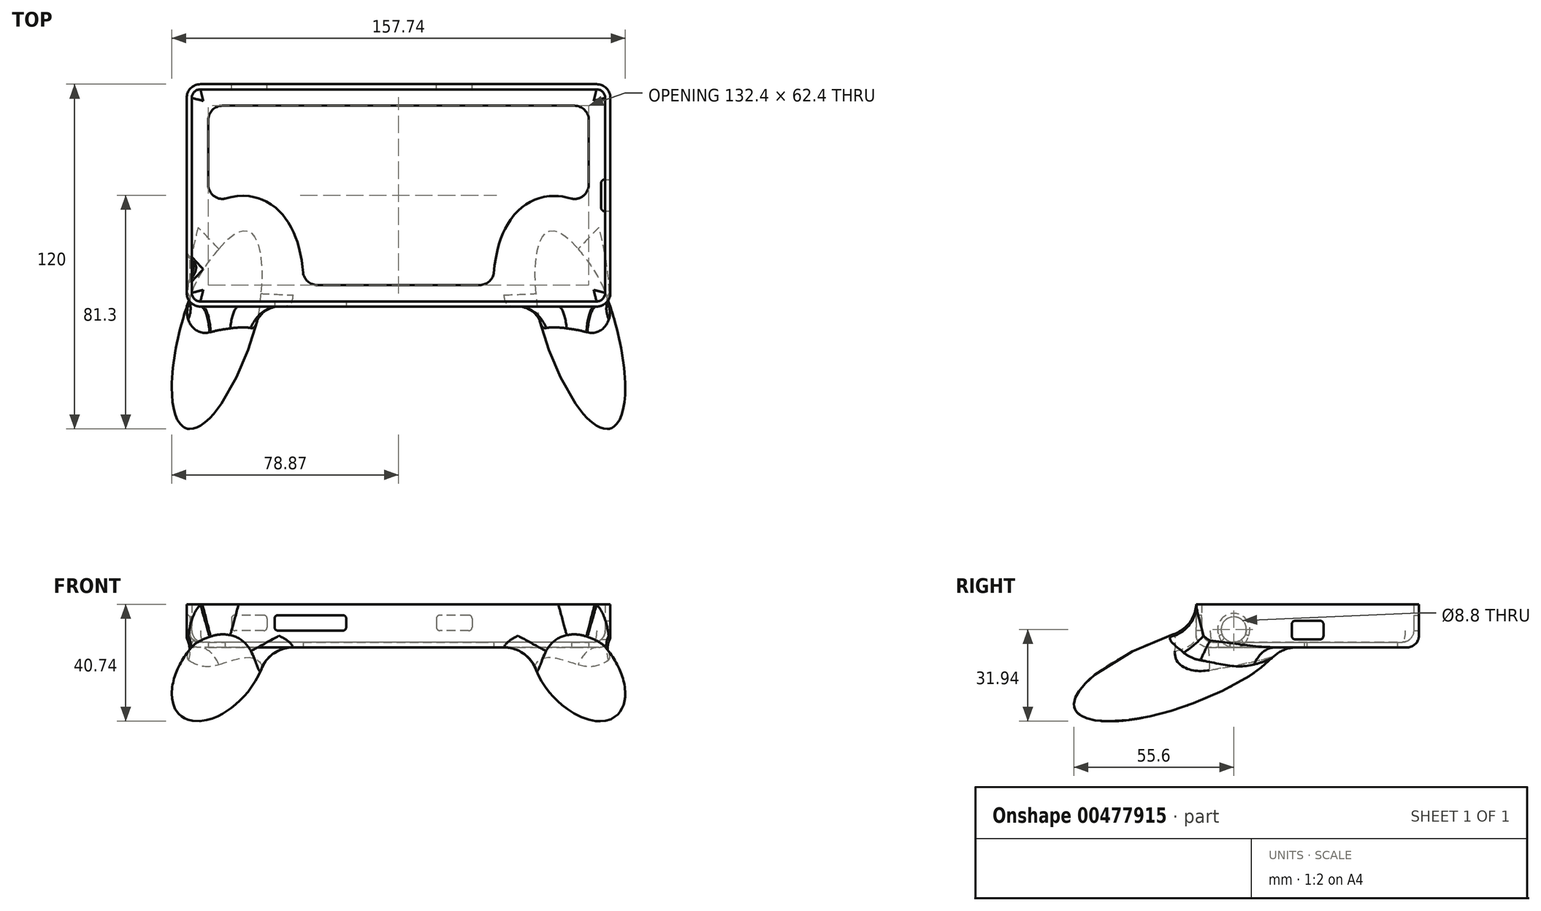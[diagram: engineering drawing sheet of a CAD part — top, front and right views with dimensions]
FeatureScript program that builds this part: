
annotation { "Feature Type Name" : "Feature", "Feature Type Description" : "" }
export const myFeature = defineFeature(function(context is Context, id is Id, definition is map)
    precondition{}
    {
        {
            var Q0;
            Q0=qCreatedBy(makeId("Top.planeOp"),FACE);
            var sketch = newSketch(context, id + "F0", { "sketchPlane" : qUnion([Q0])});
            skLineSegment(sketch, "E0.bottom", {"start": v(68.9, -36.9) * mm, "end": v(-68.9, -36.9) * mm});
            skLineSegment(sketch, "E0.top", {"start": v(68.9, 36.9) * mm, "end": v(-68.9, 36.9) * mm});
            skLineSegment(sketch, "E0.left", {"start": v(71.9, -33.9) * mm, "end": v(71.9, 33.9) * mm});
            skLineSegment(sketch, "E0.right", {"start": v(-71.9, -33.9) * mm, "end": v(-71.9, 33.9) * mm});
            skPoint(sketch, "E0.middle", {"position": v(0, 0) * mm});
            skLineSegment(sketch, "E1.bottom", {"start": v(-56.9, 37.9) * mm, "end": v(-46.9, 37.9) * mm});
            skLineSegment(sketch, "E1.top", {"start": v(-56.9, 36.9) * mm, "end": v(-46.9, 36.9) * mm});
            skLineSegment(sketch, "E1.left", {"start": v(-56.9, 37.9) * mm, "end": v(-56.9, 36.9) * mm});
            skLineSegment(sketch, "E1.right", {"start": v(-46.9, 37.9) * mm, "end": v(-46.9, 36.9) * mm});
            skLineSegment(sketch, "E2.bottom", {"start": v(14.4, 37.9) * mm, "end": v(24.4, 37.9) * mm});
            skLineSegment(sketch, "E2.top", {"start": v(14.4, 36.9) * mm, "end": v(24.4, 36.9) * mm});
            skLineSegment(sketch, "E2.left", {"start": v(14.4, 37.9) * mm, "end": v(14.4, 36.9) * mm});
            skLineSegment(sketch, "E2.right", {"start": v(24.4, 37.9) * mm, "end": v(24.4, 36.9) * mm});
            skLineSegment(sketch, "E3.bottom", {"start": v(-41.9, -36.9) * mm, "end": v(-19.4, -36.9) * mm});
            skLineSegment(sketch, "E3.top", {"start": v(-41.9, -37.9) * mm, "end": v(-19.4, -37.9) * mm});
            skLineSegment(sketch, "E3.left", {"start": v(-41.9, -36.9) * mm, "end": v(-41.9, -37.9) * mm});
            skLineSegment(sketch, "E3.right", {"start": v(-19.4, -36.9) * mm, "end": v(-19.4, -37.9) * mm});
            skPoint(sketch, "E4.visualSharp", {"position": v(71.9, 36.9) * mm});
            skArc(sketch, "E4.filletArc", {"start": v(71.9, 33.9) * mm, "mid": v(71.02, 36.02) * mm, "end": v(68.9, 36.9) * mm});
            skPoint(sketch, "E5.visualSharp", {"position": v(-71.9, 36.9) * mm});
            skArc(sketch, "E5.filletArc", {"start": v(-68.9, 36.9) * mm, "mid": v(-71.02, 36.02) * mm, "end": v(-71.9, 33.9) * mm});
            skPoint(sketch, "E6.visualSharp", {"position": v(-71.9, -36.9) * mm});
            skArc(sketch, "E6.filletArc", {"start": v(-71.9, -33.9) * mm, "mid": v(-71.02, -36.02) * mm, "end": v(-68.9, -36.9) * mm});
            skPoint(sketch, "E7.visualSharp", {"position": v(71.9, -36.9) * mm});
            skArc(sketch, "E7.filletArc", {"start": v(68.9, -36.9) * mm, "mid": v(71.02, -36.02) * mm, "end": v(71.9, -33.9) * mm});
            skSolve(sketch);
        }
        {
            var Q0;
            Q0=qCreatedBy(makeId("Top.planeOp"),FACE);
            var sketch = newSketch(context, id + "F1", { "sketchPlane" : qUnion([Q0])});
            skLineSegment(sketch, "E8", {"start": v(-71.9, -33.9) * mm, "end": v(-57.84, 4.74) * mm, "construction": true});
            skLineSegment(sketch, "E9", {"start": v(-73.64, -83.73) * mm, "end": v(-51.33, -6.9) * mm});
            skEllipticalArc(sketch, "E10", {});
            skEllipticalArc(sketch, "E11", {"construction": true});
            skEllipticalArc(sketch, "E12.MirrorCS", {});
            skLineSegment(sketch, "E13.MirrorCS", {"start": v(73.64, -83.73) * mm, "end": v(51.33, -6.9) * mm});
            skEllipticalArc(sketch, "E14.MirrorCS", {"construction": true});
            const initialGuessF1  = {"E10": [-0.062483445005433624, -0.045313524145155444, -0.27883817299371894, -0.960338103628886, 0.04, 0.0125, 3.141592653589793, 0], "E11": [-0.06248344500543363, -0.045313524145155444, -0.27883817299371894, -0.960338103628886, 0.04, 0.0125, 0, 3.141592653589793], "E12.MirrorCS": [0.06248344500543363, -0.045313524145155444, 0.27883817299371894, -0.960338103628886, 0.04, 0.0125, 0, 3.141592653589793], "E14.MirrorCS": [0.06248344500543364, -0.045313524145155444, 0.27883817299371894, -0.960338103628886, 0.04, 0.0125, 3.141592653589793, 0]};
            skSetInitialGuess(sketch, initialGuessF1);
            skSolve(sketch);
        }
        {
            var Q0;
            Q0=makeQuery(id+"F1.imprint","IMPRINT",FACE,{"disambiguationData":[TD([[makeQuery(id+"F1.imprint","IMPRINT",EDGE,{"derivedFrom":sQuery(id+"F1.wireOp",EDGE,"E9")}),1.0]])]});
            var Q1;
            Q1=sQuery(id+"F1.wireOp",EDGE,"E9");
            revolve(context, id + "F2", {"entities" : qUnion([Q0]), "axis" : qUnion([Q1]), "revolveType" : RevolveType.FULL});
        }
        {
            var Q0;
            Q0=makeQuery(id+"F1.imprint","IMPRINT",FACE,{"disambiguationData":[TD([[makeQuery(id+"F1.imprint","IMPRINT",EDGE,{"derivedFrom":sQuery(id+"F1.wireOp",EDGE,"E12.MirrorCS")}),1.0]])]});
            var Q1;
            Q1=sQuery(id+"F1.wireOp",EDGE,"E13.MirrorCS");
            revolve(context, id + "F3", {"entities" : qUnion([Q0]), "axis" : qUnion([Q1]), "revolveType" : RevolveType.FULL});
        }
        {
            var Q0;
            Q0=makeQuery(id+"F3.opRevolve","SWEPT_BODY",BODY,{"disambiguationData":[OSD([sQuery(id+"F1.wireOp",EDGE,"E12.MirrorCS"),sQuery(id+"F1.wireOp",EDGE,"E13.MirrorCS")])]});
            var Q1;
            Q1=makeQuery(id+"F2.opRevolve","SWEPT_BODY",BODY,{"disambiguationData":[OSD([sQuery(id+"F1.wireOp",EDGE,"E9"),sQuery(id+"F1.wireOp",EDGE,"E10")])]});
            var Q2;
            Q2=sQuery(id+"F0.wireOp",EDGE,"E0.bottom");
            transform(context, id + "F4", {"entities" : qUnion([Q0, Q1]), "transformType" : TransformType.ROTATION, "transformAxis" : qUnion([Q2]), "angle" : 20 * degree, "oppositeDirection" : true, "makeCopy" : false});
        }
        {
            var Q0;
            Q0=makeQuery(id+"F2.opRevolve","SWEPT_BODY",BODY,{"disambiguationData":[OSD([sQuery(id+"F1.wireOp",EDGE,"E9"),sQuery(id+"F1.wireOp",EDGE,"E10")])]});
            var Q1;
            Q1=makeQuery(id+"F3.opRevolve","SWEPT_BODY",BODY,{"disambiguationData":[OSD([sQuery(id+"F1.wireOp",EDGE,"E12.MirrorCS"),sQuery(id+"F1.wireOp",EDGE,"E13.MirrorCS")])]});
            transform(context, id + "F5", {"entities" : qUnion([Q0, Q1]), "transformType" : TransformType.TRANSLATION_3D, "dx" : 0 * mm, "dy" : 0 * mm, "dz" : -7 * mm, "makeCopy" : false});
        }
        {
            var Q0;
            {var subQ3=sQuery(id+"F0.wireOp",EDGE,"E0.left");Q0=makeQuery(id+"F0.imprint","IMPRINT",FACE,{"disambiguationData":[TD([[makeQuery(id+"F0.imprint","IMPRINT",EDGE,{"derivedFrom":subQ3}),1.0]])]});}
            extrude(context, id + "F6", {"entities" : qUnion([Q0]), "depth" : 13.2 * mm});
        }
        {
            var Q0;
            {var subQ3=sQuery(id+"F0.wireOp",EDGE,"E0.left");Q0=makeQuery(id+"F0.imprint","IMPRINT",FACE,{"disambiguationData":[TD([[makeQuery(id+"F0.imprint","IMPRINT",EDGE,{"derivedFrom":subQ3}),1.0]])]});}
            var sketch = newSketch(context, id + "F7", { "sketchPlane" : qUnion([Q0])});
            skArc(sketch, "E15.0", {"start": v(73.7, 33.9) * mm, "mid": v(72.3, 37.3) * mm, "end": v(68.9, 38.7) * mm});
            skLineSegment(sketch, "E15.1", {"start": v(73.7, -33.9) * mm, "end": v(73.7, 33.9) * mm});
            skLineSegment(sketch, "E15.2", {"start": v(68.9, 38.7) * mm, "end": v(-68.9, 38.7) * mm});
            skArc(sketch, "E15.3", {"start": v(68.9, -38.7) * mm, "mid": v(72.3, -37.3) * mm, "end": v(73.7, -33.9) * mm});
            skArc(sketch, "E15.4", {"start": v(-68.9, 38.7) * mm, "mid": v(-72.3, 37.3) * mm, "end": v(-73.7, 33.9) * mm});
            skLineSegment(sketch, "E15.5", {"start": v(-73.7, -33.9) * mm, "end": v(-73.7, 33.9) * mm});
            skArc(sketch, "E15.6", {"start": v(-73.7, -33.9) * mm, "mid": v(-72.3, -37.3) * mm, "end": v(-68.9, -38.7) * mm});
            skLineSegment(sketch, "E15.7", {"start": v(68.9, -38.7) * mm, "end": v(-68.9, -38.7) * mm});
            skSolve(sketch);
        }
        {
            var Q0;
            Q0 = qSketchRegion(id + "F7", true);
            var Q1;
            Q1=makeQuery(id+"F6.opExtrude","CAP_FACE",FACE,{"disambiguationData":[OSD([sQuery(id+"F0.wireOp",EDGE,"E0.bottom"),sQuery(id+"F0.wireOp",EDGE,"E0.top"),sQuery(id+"F0.wireOp",EDGE,"E0.left"),sQuery(id+"F0.wireOp",EDGE,"E0.right"),sQuery(id+"F0.wireOp",EDGE,"E1.top"),sQuery(id+"F0.wireOp",EDGE,"E2.top"),sQuery(id+"F0.wireOp",EDGE,"E3.bottom"),sQuery(id+"F0.wireOp",EDGE,"E4.filletArc"),sQuery(id+"F0.wireOp",EDGE,"E5.filletArc"),sQuery(id+"F0.wireOp",EDGE,"E6.filletArc"),sQuery(id+"F0.wireOp",EDGE,"E7.filletArc")])],"isStart":false});
            extrude(context, id + "F8", {"entities" : qUnion([Q0]), "endBound" : BoundingType.UP_TO_SURFACE, "endBoundEntityFace" : qUnion([Q1]), "depth" : 13 * mm, "hasSecondDirection" : true, "secondDirectionOppositeDirection" : true, "secondDirectionDepth" : 1.8 * mm});
        }
        {
            var Q0;
            Q0=makeQuery(id+"F2.opRevolve","SWEPT_BODY",BODY,{"disambiguationData":[OSD([sQuery(id+"F1.wireOp",EDGE,"E9"),sQuery(id+"F1.wireOp",EDGE,"E10")])]});
            var Q1;
            Q1=makeQuery(id+"F3.opRevolve","SWEPT_BODY",BODY,{"disambiguationData":[OSD([sQuery(id+"F1.wireOp",EDGE,"E12.MirrorCS"),sQuery(id+"F1.wireOp",EDGE,"E13.MirrorCS")])]});
            var Q2;
            Q2=makeQuery(id+"F8.opExtrude","SWEPT_BODY",BODY,{"disambiguationData":[OSD([sQuery(id+"F7.wireOp",EDGE,"E15.0"),sQuery(id+"F7.wireOp",EDGE,"E15.1"),sQuery(id+"F7.wireOp",EDGE,"E15.2"),sQuery(id+"F7.wireOp",EDGE,"E15.3"),sQuery(id+"F7.wireOp",EDGE,"E15.4"),sQuery(id+"F7.wireOp",EDGE,"E15.5"),sQuery(id+"F7.wireOp",EDGE,"E15.6"),sQuery(id+"F7.wireOp",EDGE,"E15.7")])]});
            booleanBodies(context, id + "F9", {"operationType" : BooleanOperationType.UNION, "tools" : qUnion([Q0, Q1, Q2])});
        }
        {
            var Q0;
            Q0=makeQuery(id+"F6.opExtrude","SWEPT_BODY",BODY,{"disambiguationData":[OSD([sQuery(id+"F0.wireOp",EDGE,"E0.bottom"),sQuery(id+"F0.wireOp",EDGE,"E0.top"),sQuery(id+"F0.wireOp",EDGE,"E0.left"),sQuery(id+"F0.wireOp",EDGE,"E0.right"),sQuery(id+"F0.wireOp",EDGE,"E1.top"),sQuery(id+"F0.wireOp",EDGE,"E2.top"),sQuery(id+"F0.wireOp",EDGE,"E3.bottom"),sQuery(id+"F0.wireOp",EDGE,"E4.filletArc"),sQuery(id+"F0.wireOp",EDGE,"E5.filletArc"),sQuery(id+"F0.wireOp",EDGE,"E6.filletArc"),sQuery(id+"F0.wireOp",EDGE,"E7.filletArc")])]});
            var Q1;
            Q1=makeQuery(id+"F2.opRevolve","SWEPT_BODY",BODY,{"disambiguationData":[OSD([sQuery(id+"F1.wireOp",EDGE,"E9"),sQuery(id+"F1.wireOp",EDGE,"E10")])]});
            var Q2;
            Q2=makeQuery(id+"F3.opRevolve","SWEPT_BODY",BODY,{"disambiguationData":[OSD([sQuery(id+"F1.wireOp",EDGE,"E12.MirrorCS"),sQuery(id+"F1.wireOp",EDGE,"E13.MirrorCS")])]});
            var Q3;
            Q3=makeQuery(id+"F8.opExtrude","SWEPT_BODY",BODY,{"disambiguationData":[OSD([sQuery(id+"F7.wireOp",EDGE,"E15.0"),sQuery(id+"F7.wireOp",EDGE,"E15.1"),sQuery(id+"F7.wireOp",EDGE,"E15.2"),sQuery(id+"F7.wireOp",EDGE,"E15.3"),sQuery(id+"F7.wireOp",EDGE,"E15.4"),sQuery(id+"F7.wireOp",EDGE,"E15.5"),sQuery(id+"F7.wireOp",EDGE,"E15.6"),sQuery(id+"F7.wireOp",EDGE,"E15.7")])]});
            booleanBodies(context, id + "F10", {"operationType" : BooleanOperationType.SUBTRACTION, "tools" : qUnion([Q0]), "targets" : qUnion([Q1, Q2, Q3])});
        }
        {
            var Q0;
            Q0=makeQuery(id+"F10.opBoolean","COPY",FACE,{"derivedFrom":makeQuery(id+"F6.opExtrude","CAP_FACE",FACE,{"disambiguationData":[OSD([sQuery(id+"F0.wireOp",EDGE,"E0.bottom"),sQuery(id+"F0.wireOp",EDGE,"E0.top"),sQuery(id+"F0.wireOp",EDGE,"E0.left"),sQuery(id+"F0.wireOp",EDGE,"E0.right"),sQuery(id+"F0.wireOp",EDGE,"E1.top"),sQuery(id+"F0.wireOp",EDGE,"E2.top"),sQuery(id+"F0.wireOp",EDGE,"E3.bottom"),sQuery(id+"F0.wireOp",EDGE,"E4.filletArc"),sQuery(id+"F0.wireOp",EDGE,"E5.filletArc"),sQuery(id+"F0.wireOp",EDGE,"E6.filletArc"),sQuery(id+"F0.wireOp",EDGE,"E7.filletArc")])],"isStart":true})});
            var Q1;
            Q1=makeQuery(id+"F8.opExtrude","CAP_EDGE",EDGE,{"disambiguationData":[OSD([sQuery(id+"F7.wireOp",EDGE,"E15.7")])],"isStart":true});
            var Q2;
            Q2=makeQuery(id+"F8.opExtrude","CAP_EDGE",EDGE,{"disambiguationData":[OSD([sQuery(id+"F7.wireOp",EDGE,"E15.2")])],"isStart":true});
            fillet(context, id + "F11", {"entities" : qUnion([Q0, Q1, Q2]), "radius" : 4 * mm, "tangentPropagation" : true, "allowEdgeOverflow" : false});
        }
        {
            var Q0;
            Q0=makeQuery(id+"F9.opBoolean","INTERSECT",EDGE,{"derivedFrom":[makeQuery(id+"F2.opRevolve","SWEPT_FACE",FACE,{"disambiguationData":[OSD([sQuery(id+"F1.wireOp",EDGE,"E10")])]}),makeQuery(id+"F8.opExtrude","CAP_FACE",FACE,{"disambiguationData":[OSD([sQuery(id+"F7.wireOp",EDGE,"E15.0"),sQuery(id+"F7.wireOp",EDGE,"E15.1"),sQuery(id+"F7.wireOp",EDGE,"E15.2"),sQuery(id+"F7.wireOp",EDGE,"E15.3"),sQuery(id+"F7.wireOp",EDGE,"E15.4"),sQuery(id+"F7.wireOp",EDGE,"E15.5"),sQuery(id+"F7.wireOp",EDGE,"E15.6"),sQuery(id+"F7.wireOp",EDGE,"E15.7")])],"isStart":true})]});
            var Q1;
            Q1=makeQuery(id+"F9.opBoolean","INTERSECT",EDGE,{"derivedFrom":[makeQuery(id+"F3.opRevolve","SWEPT_FACE",FACE,{"disambiguationData":[OSD([sQuery(id+"F1.wireOp",EDGE,"E12.MirrorCS")])]}),makeQuery(id+"F8.opExtrude","CAP_FACE",FACE,{"disambiguationData":[OSD([sQuery(id+"F7.wireOp",EDGE,"E15.0"),sQuery(id+"F7.wireOp",EDGE,"E15.1"),sQuery(id+"F7.wireOp",EDGE,"E15.2"),sQuery(id+"F7.wireOp",EDGE,"E15.3"),sQuery(id+"F7.wireOp",EDGE,"E15.4"),sQuery(id+"F7.wireOp",EDGE,"E15.5"),sQuery(id+"F7.wireOp",EDGE,"E15.6"),sQuery(id+"F7.wireOp",EDGE,"E15.7")])],"isStart":true})]});
            fillet(context, id + "F12", {"entities" : qUnion([Q0, Q1]), "radius" : 12 * mm, "tangentPropagation" : true, "allowEdgeOverflow" : false});
        }
        {
            var Q0;
            Q0=makeQuery(id+"F8.opExtrude","CAP_FACE",FACE,{"disambiguationData":[OSD([sQuery(id+"F7.wireOp",EDGE,"E15.0"),sQuery(id+"F7.wireOp",EDGE,"E15.1"),sQuery(id+"F7.wireOp",EDGE,"E15.2"),sQuery(id+"F7.wireOp",EDGE,"E15.3"),sQuery(id+"F7.wireOp",EDGE,"E15.4"),sQuery(id+"F7.wireOp",EDGE,"E15.5"),sQuery(id+"F7.wireOp",EDGE,"E15.6"),sQuery(id+"F7.wireOp",EDGE,"E15.7")])],"isStart":true});
            var sketch = newSketch(context, id + "F13", { "sketchPlane" : qUnion([Q0])});
            skLineSegment(sketch, "E16.0", {"start": v(66.2, -26.2) * mm, "end": v(66.2, -3.77) * mm});
            skLineSegment(sketch, "E16.1", {"start": v(28.26, 31.2) * mm, "end": v(-28.26, 31.2) * mm});
            skFitSpline(sketch, "E16.2", {"points": [v(-33.12, 34.86) * mm, v(-33.06, 33.6) * mm, v(-33.02, 31.71) * mm, v(-33.08, 29.18) * mm, v(-33.18, 27.27) * mm, v(-33.35, 25.36) * mm, v(-33.66, 22.82) * mm, v(-34.11, 20.28) * mm, v(-34.75, 17.76) * mm, v(-35.23, 16.18) * mm, v(-35.67, 14.92) * mm, v(-36.16, 13.66) * mm, v(-36.84, 12.11) * mm, v(-37.8, 10.3) * mm, v(-38.73, 8.83) * mm, v(-39.56, 7.7) * mm, v(-40.24, 6.85) * mm, v(-40.96, 6.05) * mm, v(-41.97, 5.01) * mm, v(-43.36, 3.82) * mm, v(-44.91, 2.77) * mm, v(-46.23, 2.05) * mm, v(-47.24, 1.58) * mm, v(-48.29, 1.17) * mm, v(-49.36, 0.83) * mm, v(-50.47, 0.56) * mm, v(-51.95, 0.3) * mm, v(-53.8, 0.15) * mm, v(-56, 0.24) * mm, v(-58.17, 0.58) * mm, v(-60.25, 1.13) * mm, v(-62.22, 1.86) * mm, v(-64.12, 2.75) * mm, v(-65.9, 3.76) * mm, v(-67.58, 4.86) * mm, v(-69.7, 6.44) * mm, v(-71.18, 7.74) * mm, v(-72.12, 8.65) * mm]});
            skFitSpline(sketch, "E16.3", {"points": [v(72.12, 8.65) * mm, v(71.65, 8.2) * mm, v(70.69, 7.3) * mm, v(69.17, 6.04) * mm, v(67.56, 4.85) * mm, v(65.86, 3.73) * mm, v(64.07, 2.73) * mm, v(62.2, 1.85) * mm, v(60.56, 1.25) * mm, v(59.18, 0.85) * mm, v(58.12, 0.6) * mm, v(57.05, 0.4) * mm, v(55.97, 0.27) * mm, v(54.87, 0.2) * mm, v(53.75, 0.18) * mm, v(52.62, 0.24) * mm, v(51.13, 0.42) * mm, v(49.67, 0.73) * mm, v(48.24, 1.19) * mm, v(47.19, 1.6) * mm, v(46.16, 2.09) * mm, v(44.85, 2.8) * mm, v(43.63, 3.64) * mm, v(42.49, 4.57) * mm, v(41.4, 5.56) * mm, v(40.18, 6.88) * mm, v(38.9, 8.56) * mm, v(37.97, 10.03) * mm, v(37.3, 11.25) * mm, v(36.68, 12.47) * mm, v(36, 14.02) * mm, v(35.31, 15.9) * mm, v(34.74, 17.8) * mm, v(34.1, 20.35) * mm, v(33.53, 23.52) * mm, v(33.15, 27.31) * mm, v(33.01, 31.09) * mm, v(33.06, 33.6) * mm, v(33.12, 34.86) * mm]});
            skLineSegment(sketch, "E16.4", {"start": v(-66.2, -3.77) * mm, "end": v(-66.2, -26.2) * mm});
            skLineSegment(sketch, "E16.5", {"start": v(-61.2, -31.2) * mm, "end": v(61.2, -31.2) * mm});
            skPoint(sketch, "E17.visualSharp", {"position": v(66.2, -31.2) * mm});
            skArc(sketch, "E17.filletArc", {"start": v(61.2, -31.2) * mm, "mid": v(64.74, -29.74) * mm, "end": v(66.2, -26.2) * mm});
            skPoint(sketch, "E18.visualSharp", {"position": v(-66.2, -31.2) * mm});
            skArc(sketch, "E18.filletArc", {"start": v(-66.2, -26.2) * mm, "mid": v(-64.74, -29.74) * mm, "end": v(-61.2, -31.2) * mm});
            skPoint(sketch, "E19.visualSharp", {"position": v(-66.2, 3.97) * mm});
            skArc(sketch, "E19.filletArc", {"start": v(-59.79, 1.03) * mm, "mid": v(-64.2, 0.23) * mm, "end": v(-66.2, -3.77) * mm});
            skPoint(sketch, "E20.visualSharp", {"position": v(-33.05, 31.2) * mm});
            skArc(sketch, "E20.filletArc", {"start": v(-28.26, 31.2) * mm, "mid": v(-31.65, 29.88) * mm, "end": v(-33.24, 26.6) * mm});
            skPoint(sketch, "E21.visualSharp", {"position": v(33.05, 31.2) * mm});
            skArc(sketch, "E21.filletArc", {"start": v(33.24, 26.6) * mm, "mid": v(31.65, 29.88) * mm, "end": v(28.26, 31.2) * mm});
            skPoint(sketch, "E22.visualSharp", {"position": v(66.2, 3.97) * mm});
            skArc(sketch, "E22.filletArc", {"start": v(66.2, -3.77) * mm, "mid": v(64.2, 0.23) * mm, "end": v(59.79, 1.03) * mm});
            skSolve(sketch);
        }
        {
            var Q0;
            Q0=makeQuery(id+"F13.imprint","IMPRINT",FACE,{"disambiguationData":[TD([[makeQuery(id+"F13.imprint","IMPRINT",EDGE,{"derivedFrom":sQuery(id+"F13.wireOp",EDGE,"E16.0")}),1.0]])]});
            extrude(context, id + "F14", {"entities" : qUnion([Q0]), "operationType" : NewBodyOperationType.REMOVE, "endBound" : BoundingType.THROUGH_ALL, "oppositeDirection" : true, "depth" : 25 * mm});
        }
        {
            var Q0;
            Q0=makeQuery(id+"F8.opExtrude","SWEPT_FACE",FACE,{"disambiguationData":[OSD([sQuery(id+"F7.wireOp",EDGE,"E15.2")])]});
            var sketch = newSketch(context, id + "F15", { "sketchPlane" : qUnion([Q0])});
            skLineSegment(sketch, "E23.bottom", {"start": v(-24.4, 8.2) * mm, "end": v(-14.4, 8.2) * mm, "construction": true});
            skLineSegment(sketch, "E23.top", {"start": v(-24.4, 5.2) * mm, "end": v(-14.4, 5.2) * mm, "construction": true});
            skLineSegment(sketch, "E23.left", {"start": v(-24.4, 8.2) * mm, "end": v(-24.4, 5.2) * mm, "construction": true});
            skLineSegment(sketch, "E23.right", {"start": v(-14.4, 8.2) * mm, "end": v(-14.4, 5.2) * mm, "construction": true});
            skLineSegment(sketch, "E24.bottom", {"start": v(46.9, 8.2) * mm, "end": v(56.9, 8.2) * mm, "construction": true});
            skLineSegment(sketch, "E24.top", {"start": v(46.9, 5.2) * mm, "end": v(56.9, 5.2) * mm, "construction": true});
            skLineSegment(sketch, "E24.left", {"start": v(46.9, 8.2) * mm, "end": v(46.9, 5.2) * mm, "construction": true});
            skLineSegment(sketch, "E24.right", {"start": v(56.9, 8.2) * mm, "end": v(56.9, 5.2) * mm, "construction": true});
            skLineSegment(sketch, "E25.0", {"start": v(-24.4, 9.4) * mm, "end": v(-14.4, 9.4) * mm});
            skLineSegment(sketch, "E25.1", {"start": v(-25.6, 8.2) * mm, "end": v(-25.6, 5.2) * mm});
            skLineSegment(sketch, "E25.2", {"start": v(-24.4, 4) * mm, "end": v(-14.4, 4) * mm});
            skLineSegment(sketch, "E25.3", {"start": v(-13.2, 8.2) * mm, "end": v(-13.2, 5.2) * mm});
            skLineSegment(sketch, "E26.0", {"start": v(45.7, 8.2) * mm, "end": v(45.7, 5.2) * mm});
            skLineSegment(sketch, "E26.1", {"start": v(46.9, 9.4) * mm, "end": v(56.9, 9.4) * mm});
            skLineSegment(sketch, "E26.2", {"start": v(58.1, 8.2) * mm, "end": v(58.1, 5.2) * mm});
            skLineSegment(sketch, "E26.3", {"start": v(46.9, 4) * mm, "end": v(56.9, 4) * mm});
            skPoint(sketch, "E27.visualSharp", {"position": v(-25.6, 9.4) * mm});
            skArc(sketch, "E27.filletArc", {"start": v(-24.4, 9.4) * mm, "mid": v(-25.25, 9.05) * mm, "end": v(-25.6, 8.2) * mm});
            skPoint(sketch, "E28.visualSharp", {"position": v(-25.6, 4) * mm});
            skArc(sketch, "E28.filletArc", {"start": v(-25.6, 5.2) * mm, "mid": v(-25.25, 4.35) * mm, "end": v(-24.4, 4) * mm});
            skPoint(sketch, "E29.visualSharp", {"position": v(-13.2, 4) * mm});
            skArc(sketch, "E29.filletArc", {"start": v(-14.4, 4) * mm, "mid": v(-13.55, 4.35) * mm, "end": v(-13.2, 5.2) * mm});
            skPoint(sketch, "E30.visualSharp", {"position": v(-13.2, 9.4) * mm});
            skArc(sketch, "E30.filletArc", {"start": v(-13.2, 8.2) * mm, "mid": v(-13.55, 9.05) * mm, "end": v(-14.4, 9.4) * mm});
            skPoint(sketch, "E31.visualSharp", {"position": v(45.7, 4) * mm});
            skArc(sketch, "E31.filletArc", {"start": v(45.7, 5.2) * mm, "mid": v(46.05, 4.35) * mm, "end": v(46.9, 4) * mm});
            skPoint(sketch, "E32.visualSharp", {"position": v(45.7, 9.4) * mm});
            skArc(sketch, "E32.filletArc", {"start": v(46.9, 9.4) * mm, "mid": v(46.05, 9.05) * mm, "end": v(45.7, 8.2) * mm});
            skPoint(sketch, "E33.visualSharp", {"position": v(58.1, 9.4) * mm});
            skArc(sketch, "E33.filletArc", {"start": v(58.1, 8.2) * mm, "mid": v(57.75, 9.05) * mm, "end": v(56.9, 9.4) * mm});
            skPoint(sketch, "E34.visualSharp", {"position": v(58.1, 4) * mm});
            skArc(sketch, "E34.filletArc", {"start": v(56.9, 4) * mm, "mid": v(57.75, 4.35) * mm, "end": v(58.1, 5.2) * mm});
            skSolve(sketch);
        }
        {
            var Q0;
            Q0 = qSketchRegion(id + "F15", true);
            var Q1;
            Q1=makeQuery(id+"F10.opBoolean","COPY",FACE,{"derivedFrom":makeQuery(id+"F6.opExtrude","SWEPT_FACE",FACE,{"disambiguationData":[OSD([sQuery(id+"F0.wireOp",EDGE,"E0.top"),sQuery(id+"F0.wireOp",EDGE,"E1.top"),sQuery(id+"F0.wireOp",EDGE,"E2.top")])]})});
            extrude(context, id + "F16", {"entities" : qUnion([Q0]), "operationType" : NewBodyOperationType.REMOVE, "endBound" : BoundingType.UP_TO_SURFACE, "oppositeDirection" : true, "endBoundEntityFace" : qUnion([Q1]), "depth" : 25 * mm});
        }
        {
            var Q0;
            Q0=makeQuery(id+"F12.opFillet","SPLIT",FACE,{"disambiguationData":[OD(2.0)],"derivedFrom":makeQuery(id+"F8.opExtrude","SWEPT_FACE",FACE,{"disambiguationData":[OSD([sQuery(id+"F7.wireOp",EDGE,"E15.7")])]})});
            var sketch = newSketch(context, id + "F17", { "sketchPlane" : qUnion([Q0])});
            skLineSegment(sketch, "E35.bottom", {"start": v(-41.9, 8.2) * mm, "end": v(-19.4, 8.2) * mm, "construction": true});
            skLineSegment(sketch, "E35.top", {"start": v(-41.9, 5.2) * mm, "end": v(-19.4, 5.2) * mm, "construction": true});
            skLineSegment(sketch, "E35.left", {"start": v(-41.9, 8.2) * mm, "end": v(-41.9, 5.2) * mm, "construction": true});
            skLineSegment(sketch, "E35.right", {"start": v(-19.4, 8.2) * mm, "end": v(-19.4, 5.2) * mm, "construction": true});
            skLineSegment(sketch, "E36.0", {"start": v(-41.9, 9.4) * mm, "end": v(-19.4, 9.4) * mm});
            skLineSegment(sketch, "E36.1", {"start": v(-43.1, 8.2) * mm, "end": v(-43.1, 5.2) * mm});
            skLineSegment(sketch, "E36.2", {"start": v(-41.9, 4) * mm, "end": v(-19.4, 4) * mm});
            skLineSegment(sketch, "E36.3", {"start": v(-18.2, 8.2) * mm, "end": v(-18.2, 5.2) * mm});
            skPoint(sketch, "E37.visualSharp", {"position": v(-43.1, 9.4) * mm});
            skArc(sketch, "E37.filletArc", {"start": v(-41.9, 9.4) * mm, "mid": v(-42.75, 9.05) * mm, "end": v(-43.1, 8.2) * mm});
            skPoint(sketch, "E38.visualSharp", {"position": v(-43.1, 4) * mm});
            skArc(sketch, "E38.filletArc", {"start": v(-43.1, 5.2) * mm, "mid": v(-42.75, 4.35) * mm, "end": v(-41.9, 4) * mm});
            skPoint(sketch, "E39.visualSharp", {"position": v(-18.2, 4) * mm});
            skArc(sketch, "E39.filletArc", {"start": v(-19.4, 4) * mm, "mid": v(-18.55, 4.35) * mm, "end": v(-18.2, 5.2) * mm});
            skPoint(sketch, "E40.visualSharp", {"position": v(-18.2, 9.4) * mm});
            skArc(sketch, "E40.filletArc", {"start": v(-18.2, 8.2) * mm, "mid": v(-18.55, 9.05) * mm, "end": v(-19.4, 9.4) * mm});
            skSolve(sketch);
        }
        {
            var Q0;
            Q0 = qSketchRegion(id + "F17", true);
            var Q1;
            Q1=makeQuery(id+"F10.opBoolean","COPY",FACE,{"derivedFrom":makeQuery(id+"F6.opExtrude","SWEPT_FACE",FACE,{"disambiguationData":[OSD([sQuery(id+"F0.wireOp",EDGE,"E0.bottom"),sQuery(id+"F0.wireOp",EDGE,"E3.bottom")])]})});
            extrude(context, id + "F18", {"entities" : qUnion([Q0]), "operationType" : NewBodyOperationType.REMOVE, "endBound" : BoundingType.UP_TO_SURFACE, "oppositeDirection" : true, "endBoundEntityFace" : qUnion([Q1]), "depth" : 25 * mm});
        }
        {
            var Q0;
            Q0=makeQuery(id+"F8.opExtrude","SWEPT_FACE",FACE,{"disambiguationData":[OSD([sQuery(id+"F7.wireOp",EDGE,"E15.1")])]});
            var sketch = newSketch(context, id + "F19", { "sketchPlane" : qUnion([Q0])});
            skLineSegment(sketch, "E41.bottom", {"start": v(4.3, 0.95) * mm, "end": v(-4.3, 0.95) * mm});
            skLineSegment(sketch, "E41.top", {"start": v(4.3, 7.45) * mm, "end": v(-4.3, 7.45) * mm});
            skLineSegment(sketch, "E41.left", {"start": v(5.5, 2.15) * mm, "end": v(5.5, 6.25) * mm});
            skLineSegment(sketch, "E41.right", {"start": v(-5.5, 2.15) * mm, "end": v(-5.5, 6.25) * mm});
            skPoint(sketch, "E41.middle", {"position": v(0, 4.2) * mm});
            skPoint(sketch, "E42.visualSharp", {"position": v(-5.5, 7.45) * mm});
            skArc(sketch, "E42.filletArc", {"start": v(-4.3, 7.45) * mm, "mid": v(-5.15, 7.1) * mm, "end": v(-5.5, 6.25) * mm});
            skPoint(sketch, "E43.visualSharp", {"position": v(5.5, 7.45) * mm});
            skArc(sketch, "E43.filletArc", {"start": v(5.5, 6.25) * mm, "mid": v(5.15, 7.1) * mm, "end": v(4.3, 7.45) * mm});
            skPoint(sketch, "E44.visualSharp", {"position": v(5.5, 0.95) * mm});
            skArc(sketch, "E44.filletArc", {"start": v(4.3, 0.95) * mm, "mid": v(5.15, 1.3) * mm, "end": v(5.5, 2.15) * mm});
            skPoint(sketch, "E45.visualSharp", {"position": v(-5.5, 0.95) * mm});
            skArc(sketch, "E45.filletArc", {"start": v(-5.5, 2.15) * mm, "mid": v(-5.15, 1.3) * mm, "end": v(-4.3, 0.95) * mm});
            skSolve(sketch);
        }
        {
            var Q0;
            Q0 = qSketchRegion(id + "F19", true);
            var Q1;
            Q1=makeQuery(id+"F10.opBoolean","COPY",FACE,{"derivedFrom":makeQuery(id+"F6.opExtrude","SWEPT_FACE",FACE,{"disambiguationData":[OSD([sQuery(id+"F0.wireOp",EDGE,"E0.left")])]})});
            var Q2;
            {var subQ0=sQuery(id+"F0.wireOp",EDGE,"E7.filletArc");var subQ1=sQuery(id+"F0.wireOp",EDGE,"E3.bottom");var subQ2=sQuery(id+"F0.wireOp",EDGE,"E0.left");var subQ3=sQuery(id+"F0.wireOp",EDGE,"E0.bottom");Q2=makeQuery(id+"F11.opFillet","BLEND_VERTEX",VERTEX,{"blendedFrom":[makeQuery(id+"F10.opBoolean","COPY",EDGE,{"derivedFrom":makeQuery(id+"F6.opExtrude","CAP_EDGE",EDGE,{"disambiguationData":[OSD([subQ3,subQ1])],"isStart":true})}),makeQuery(id+"F10.opBoolean","COPY",EDGE,{"derivedFrom":makeQuery(id+"F6.opExtrude","CAP_EDGE",EDGE,{"disambiguationData":[OSD([subQ2])],"isStart":true})}),makeQuery(id+"F10.opBoolean","COPY",EDGE,{"derivedFrom":makeQuery(id+"F6.opExtrude","CAP_EDGE",EDGE,{"disambiguationData":[OSD([subQ0])],"isStart":true})}),makeQuery(id+"F10.opBoolean","COPY",FACE,{"derivedFrom":makeQuery(id+"F6.opExtrude","CAP_FACE",FACE,{"disambiguationData":[OSD([subQ3,sQuery(id+"F0.wireOp",EDGE,"E0.top"),subQ2,sQuery(id+"F0.wireOp",EDGE,"E0.right"),sQuery(id+"F0.wireOp",EDGE,"E1.top"),sQuery(id+"F0.wireOp",EDGE,"E2.top"),subQ1,sQuery(id+"F0.wireOp",EDGE,"E4.filletArc"),sQuery(id+"F0.wireOp",EDGE,"E5.filletArc"),sQuery(id+"F0.wireOp",EDGE,"E6.filletArc"),subQ0])],"isStart":true})})],"blendedInto":[makeQuery(id+"F10.opBoolean","COPY",FACE,{"derivedFrom":makeQuery(id+"F6.opExtrude","CAP_FACE",FACE,{"disambiguationData":[OSD([subQ3,sQuery(id+"F0.wireOp",EDGE,"E0.top"),subQ2,sQuery(id+"F0.wireOp",EDGE,"E0.right"),sQuery(id+"F0.wireOp",EDGE,"E1.top"),sQuery(id+"F0.wireOp",EDGE,"E2.top"),subQ1,sQuery(id+"F0.wireOp",EDGE,"E4.filletArc"),sQuery(id+"F0.wireOp",EDGE,"E5.filletArc"),sQuery(id+"F0.wireOp",EDGE,"E6.filletArc"),subQ0])],"isStart":true})})]});}
            extrude(context, id + "F20", {"entities" : qUnion([Q0]), "operationType" : NewBodyOperationType.REMOVE, "endBound" : BoundingType.UP_TO_VERTEX, "oppositeDirection" : true, "endBoundEntityFace" : qUnion([Q1]), "endBoundEntityVertex" : qUnion([Q2]), "depth" : 25 * mm});
        }
        {
            var Q0;
            Q0=makeQuery(id+"F8.opExtrude","SWEPT_FACE",FACE,{"disambiguationData":[OSD([sQuery(id+"F7.wireOp",EDGE,"E15.5")])]});
            var sketch = newSketch(context, id + "F21", { "sketchPlane" : qUnion([Q0])});
            skCircle(sketch, "E46", {"center": v(25.7, 4.4) * mm, "radius": 1.9 * mm, "construction": true});
            skLineSegment(sketch, "E47.0", {"start": v(-32.9, 0) * mm, "end": v(32.9, 0) * mm, "construction": true});
            skCircle(sketch, "E48", {"center": v(25.7, 4.4) * mm, "radius": 4.4 * mm});
            skLineSegment(sketch, "E49.0", {"start": v(38.7, 8.2) * mm, "end": v(38.7, 5.2) * mm, "construction": true});
            skSolve(sketch);
        }
        {
            var Q0;
            {var subQ0=sQuery(id+"F21.wireOp",EDGE,"E48");var subQ1=sQuery(id+"F7.wireOp",EDGE,"E15.5");var subQ2=makeQuery(id+"F11.opFillet","BLEND_EDGE",EDGE,{"blendedFrom":[makeQuery(id+"F8.opExtrude","CAP_EDGE",EDGE,{"disambiguationData":[OSD([subQ1])],"isStart":true}),makeQuery(id+"F8.opExtrude","SWEPT_FACE",FACE,{"disambiguationData":[OSD([subQ1])]})],"blendedInto":[makeQuery(id+"F8.opExtrude","SWEPT_FACE",FACE,{"disambiguationData":[OSD([subQ1])]})]});var subQ3=makeQuery(id+"F21.imprint","INTERSECT",VERTEX,{"disambiguationData":[OD(0.0)],"derivedFrom":[subQ2,subQ0]});Q0=makeQuery(id+"F21.imprint","IMPRINT",FACE,{"disambiguationData":[TD([[makeQuery(id+"F21.imprint","IMPRINT",EDGE,{"disambiguationData":[TD([[subQ3,-1.0]])],"derivedFrom":subQ0}),1.0]])]});}
            var Q1;
            {var subQ0=sQuery(id+"F21.wireOp",EDGE,"E48");var subQ1=sQuery(id+"F7.wireOp",EDGE,"E15.5");var subQ2=makeQuery(id+"F11.opFillet","BLEND_EDGE",EDGE,{"blendedFrom":[makeQuery(id+"F8.opExtrude","CAP_EDGE",EDGE,{"disambiguationData":[OSD([subQ1])],"isStart":true}),makeQuery(id+"F8.opExtrude","SWEPT_FACE",FACE,{"disambiguationData":[OSD([subQ1])]})],"blendedInto":[makeQuery(id+"F8.opExtrude","SWEPT_FACE",FACE,{"disambiguationData":[OSD([subQ1])]})]});var subQ3=makeQuery(id+"F21.imprint","INTERSECT",VERTEX,{"disambiguationData":[OD(0.0)],"derivedFrom":[subQ2,subQ0]});Q1=makeQuery(id+"F21.imprint","IMPRINT",FACE,{"disambiguationData":[TD([[makeQuery(id+"F21.imprint","IMPRINT",EDGE,{"disambiguationData":[TD([[subQ3,1.0]])],"derivedFrom":subQ0}),1.0]])]});}
            var Q2;
            {var subQ0=sQuery(id+"F0.wireOp",EDGE,"E6.filletArc");var subQ1=sQuery(id+"F0.wireOp",EDGE,"E3.bottom");var subQ2=sQuery(id+"F0.wireOp",EDGE,"E0.right");var subQ3=sQuery(id+"F0.wireOp",EDGE,"E0.bottom");Q2=makeQuery(id+"F11.opFillet","BLEND_VERTEX",VERTEX,{"blendedFrom":[makeQuery(id+"F10.opBoolean","COPY",EDGE,{"derivedFrom":makeQuery(id+"F6.opExtrude","CAP_EDGE",EDGE,{"disambiguationData":[OSD([subQ3,subQ1])],"isStart":true})}),makeQuery(id+"F10.opBoolean","COPY",EDGE,{"derivedFrom":makeQuery(id+"F6.opExtrude","CAP_EDGE",EDGE,{"disambiguationData":[OSD([subQ2])],"isStart":true})}),makeQuery(id+"F10.opBoolean","COPY",EDGE,{"derivedFrom":makeQuery(id+"F6.opExtrude","CAP_EDGE",EDGE,{"disambiguationData":[OSD([subQ0])],"isStart":true})}),makeQuery(id+"F10.opBoolean","COPY",FACE,{"derivedFrom":makeQuery(id+"F6.opExtrude","CAP_FACE",FACE,{"disambiguationData":[OSD([subQ3,sQuery(id+"F0.wireOp",EDGE,"E0.top"),sQuery(id+"F0.wireOp",EDGE,"E0.left"),subQ2,sQuery(id+"F0.wireOp",EDGE,"E1.top"),sQuery(id+"F0.wireOp",EDGE,"E2.top"),subQ1,sQuery(id+"F0.wireOp",EDGE,"E4.filletArc"),sQuery(id+"F0.wireOp",EDGE,"E5.filletArc"),subQ0,sQuery(id+"F0.wireOp",EDGE,"E7.filletArc")])],"isStart":true})})],"blendedInto":[makeQuery(id+"F10.opBoolean","COPY",FACE,{"derivedFrom":makeQuery(id+"F6.opExtrude","CAP_FACE",FACE,{"disambiguationData":[OSD([subQ3,sQuery(id+"F0.wireOp",EDGE,"E0.top"),sQuery(id+"F0.wireOp",EDGE,"E0.left"),subQ2,sQuery(id+"F0.wireOp",EDGE,"E1.top"),sQuery(id+"F0.wireOp",EDGE,"E2.top"),subQ1,sQuery(id+"F0.wireOp",EDGE,"E4.filletArc"),sQuery(id+"F0.wireOp",EDGE,"E5.filletArc"),subQ0,sQuery(id+"F0.wireOp",EDGE,"E7.filletArc")])],"isStart":true})})]});}
            extrude(context, id + "F22", {"entities" : qUnion([Q0, Q1]), "operationType" : NewBodyOperationType.REMOVE, "endBound" : BoundingType.UP_TO_VERTEX, "oppositeDirection" : true, "depth" : 25 * mm, "endBoundEntityVertex" : qUnion([Q2]), "offsetDistance" : 25 * mm});
        }
        {
            var Q0;
            Q0=makeQuery(id+"F18.boolean.opBoolean","COPY",EDGE,{"derivedFrom":makeQuery(id+"F18.opExtrude","CAP_EDGE",EDGE,{"disambiguationData":[OSD([sQuery(id+"F17.wireOp",EDGE,"E36.0")])],"isStart":true})});
            var Q1;
            Q1=makeQuery(id+"F16.boolean.opBoolean","COPY",EDGE,{"derivedFrom":makeQuery(id+"F16.opExtrude","CAP_EDGE",EDGE,{"disambiguationData":[OSD([sQuery(id+"F15.wireOp",EDGE,"E26.1")])],"isStart":true})});
            var Q2;
            Q2=makeQuery(id+"F16.boolean.opBoolean","COPY",EDGE,{"derivedFrom":makeQuery(id+"F16.opExtrude","CAP_EDGE",EDGE,{"disambiguationData":[OSD([sQuery(id+"F15.wireOp",EDGE,"E25.0")])],"isStart":true})});
            var Q3;
            Q3=makeQuery(id+"F14.boolean.opBoolean","COPY",EDGE,{"derivedFrom":makeQuery(id+"F14.opExtrude","CAP_EDGE",EDGE,{"disambiguationData":[OSD([sQuery(id+"F13.wireOp",EDGE,"E16.5")])],"isStart":true})});
            var Q4;
            Q4=makeQuery(id+"F20.boolean.opBoolean","COPY",EDGE,{"derivedFrom":makeQuery(id+"F20.opExtrude","CAP_EDGE",EDGE,{"disambiguationData":[OSD([sQuery(id+"F19.wireOp",EDGE,"E41.top")])],"isStart":true})});
            var Q5;
            Q5=makeQuery(id+"F22.boolean.opBoolean","INTERSECT",EDGE,{"derivedFrom":[makeQuery(id+"F11.opFillet","BLEND_FACE",FACE,{"disambiguationData":[OSD([sQuery(id+"F7.wireOp",EDGE,"E15.5")]),OD(0.0)]}),makeQuery(id+"F22.opExtrude","SWEPT_FACE",FACE,{"disambiguationData":[OSD([sQuery(id+"F21.wireOp",EDGE,"E48")])]})]});
            chamfer(context, id + "F23", {"entities" : qUnion([Q0, Q1, Q2, Q3, Q4, Q5]), "width" : 1.2 * mm, "tangentPropagation" : true});
        }
    });
